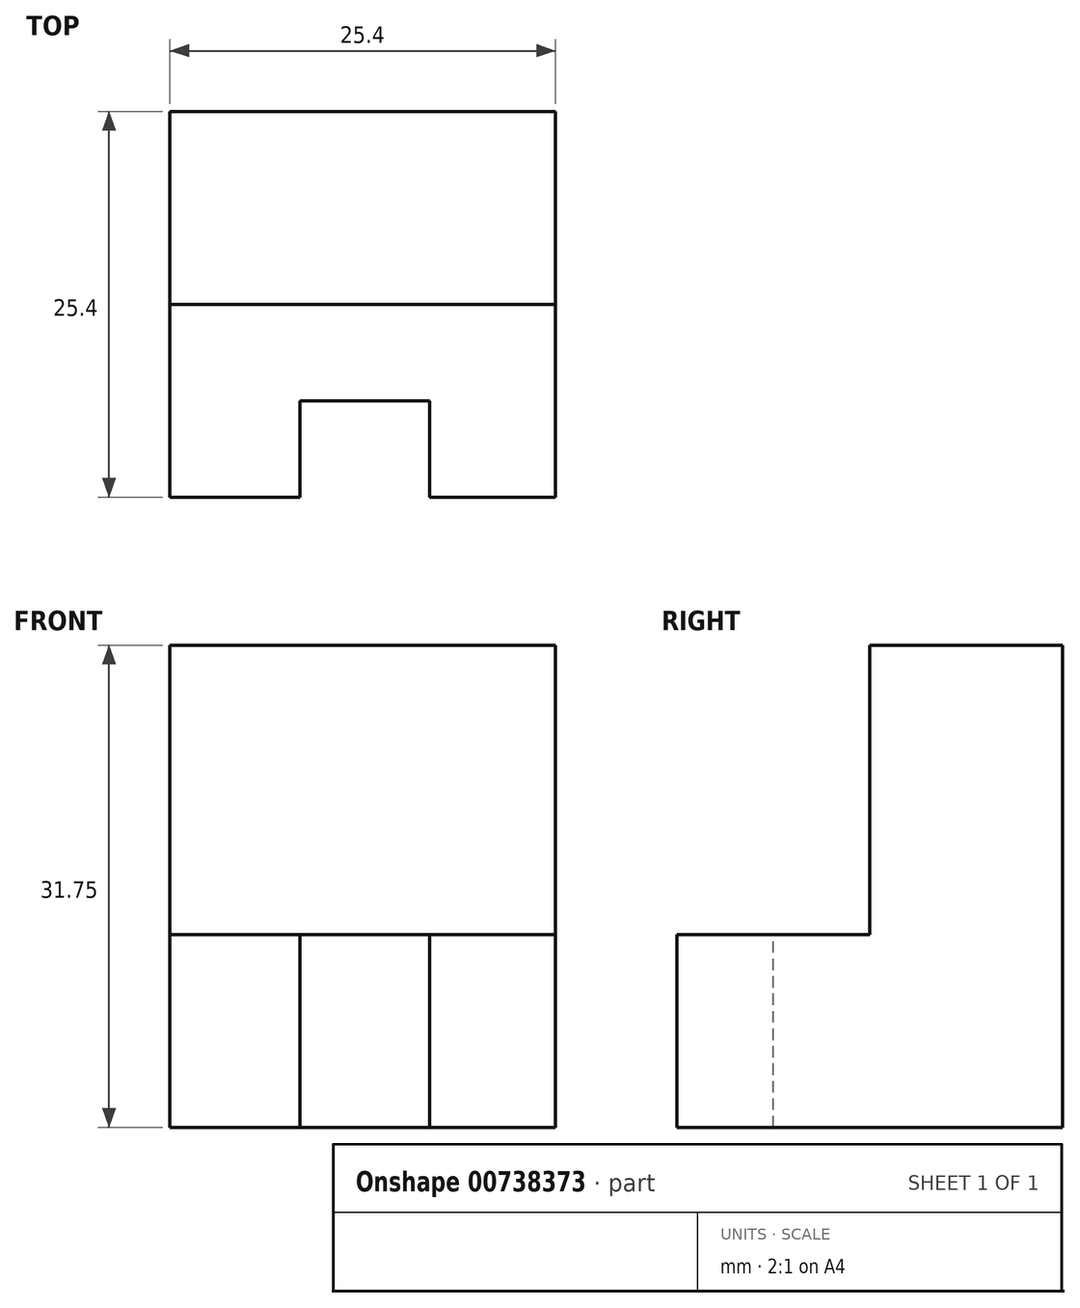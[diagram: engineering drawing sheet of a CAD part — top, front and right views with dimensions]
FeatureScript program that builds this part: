
annotation { "Feature Type Name" : "Feature", "Feature Type Description" : "" }
export const myFeature = defineFeature(function(context is Context, id is Id, definition is map)
    precondition{}
    {
        {
            var Q0;
            Q0=qCreatedBy(makeId("Right.planeOp"),FACE);
            var sketch = newSketch(context, id + "F0", { "sketchPlane" : qUnion([Q0])});
            skLineSegment(sketch, "E0", {"start": v(0, 0) * mm, "end": v(25.4, 0) * mm});
            skLineSegment(sketch, "E1", {"start": v(25.4, 0) * mm, "end": v(25.4, 31.75) * mm});
            skLineSegment(sketch, "E2", {"start": v(25.4, 31.75) * mm, "end": v(12.7, 31.75) * mm});
            skLineSegment(sketch, "E3", {"start": v(12.7, 31.75) * mm, "end": v(12.7, 12.7) * mm});
            skLineSegment(sketch, "E4", {"start": v(12.7, 12.7) * mm, "end": v(0, 12.7) * mm});
            skLineSegment(sketch, "E5", {"start": v(0, 12.7) * mm, "end": v(0, 0) * mm});
            skSolve(sketch);
        }
        {
            var Q0;
            Q0=makeQuery(id+"F0.imprint","IMPRINT",FACE,{"disambiguationData":[TD([[makeQuery(id+"F0.imprint","IMPRINT",EDGE,{"derivedFrom":sQuery(id+"F0.wireOp",EDGE,"E0")}),1.0]])]});
            extrude(context, id + "F1", {"entities" : qUnion([Q0]), "depth" : 25.4 * mm, "offsetDistance" : 25.4 * mm});
        }
        {
            var Q0;
            Q0=makeQuery(id+"F1.opExtrude","SWEPT_FACE",FACE,{"disambiguationData":[OSD([sQuery(id+"F0.wireOp",EDGE,"E4")])]});
            var sketch = newSketch(context, id + "F2", { "sketchPlane" : qUnion([Q0])});
            skLineSegment(sketch, "E6", {"start": v(17.1, 0) * mm, "end": v(17.1, 6.35) * mm});
            skPoint(sketch, "E6.endSnap0", {"position": v(25.4, 6.35) * mm});
            skLineSegment(sketch, "E7", {"start": v(17.1, 6.35) * mm, "end": v(8.55, 6.35) * mm});
            skLineSegment(sketch, "E8", {"start": v(8.55, 6.35) * mm, "end": v(8.55, 0) * mm});
            skSolve(sketch);
        }
        {
            var Q0;
            {var subQ0=sQuery(id+"F2.wireOp",EDGE,"E6");Q0=makeQuery(id+"F2.imprint","IMPRINT",FACE,{"disambiguationData":[TD([[makeQuery(id+"F2.imprint","IMPRINT",EDGE,{"derivedFrom":subQ0}),1.0]])]});}
            extrude(context, id + "F3", {"entities" : qUnion([Q0]), "operationType" : NewBodyOperationType.REMOVE, "oppositeDirection" : true, "depth" : 25.4 * mm, "offsetDistance" : 25.4 * mm});
        }
    });
